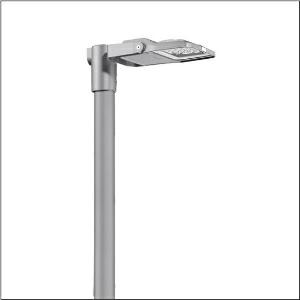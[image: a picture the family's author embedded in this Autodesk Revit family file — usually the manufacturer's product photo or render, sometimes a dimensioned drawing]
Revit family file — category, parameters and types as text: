
# Revit family: floodlight_fl_21_iq_micro___pl61_5xa7762a4c3a_196d
name_source: partatom
category: Lighting Fixtures
units: mm (PartAtom-declared; Revit-internal decimal feet)

## family parameters
Cut with Voids When Loaded = No
Host = Face
Light Source = No
Part Type = Normal
Room Calculation Point = No
Round Connector Dimension = Use Diameter
Shared = No

## types (1)
- --- (1 x LED, 3030 lm, 23.1 W, 4000K)
    Apparent Load = 23 VA
    CIE Flux Codes = 33 65 98 100 100
    Color Rendering = 70
    Color Temperature = 4000K
    Default Elevation = 1800 mm
    Description = Floodlight FL 21 iQ micro, floodlight, primary light control with lens, of PMMA, primary optical cover: protective disc, of toughened safety glass, transparent, light distribution: PL61, light emission: direct distribution, installation type: surface-mounted, lamps: LED, High Power LED, rated values: 3.030lm | 23,1W | 131,2lm/W (begin service life); end service life: 3.030lm | 23,8W; at 50% lumin. flux: 1.515lm | 11W | 137,7lm/W, colour temperature: 4000K, colour rendering: CRI > 70, light colour: 740, light setting 1 begin service life: 100% | 3.030lm | 23,1W | 131,2lm/W | 4.000K, light setting 1 end service life: 23,8W, further light settings possible, control: Auto-Match, Temp-Guard, Night-Set, Smart-Wire, Desk-Remote (wireless, voltage-free reading and setting of iQ features in the workshop via application-optimized NFC function/RFID function), optimised constant luminous flux control (CLO 2.0), Street-Remote, pre-setting: linear dimming characteristic, with terminal, 6-pole, mains connection: 220..240V, AC, 50/60Hz, luminaire housing, of diecast aluminium, powder-coated, SITECO metallic grey (DB 702S), corrosivity category C5 mid according to DIN EN ISO 12944suitable for swimming poolschlorine-resistant, sealing non-destructively replaceable, please order mast flange separately, mast bracket, of steel, galvanised, powder-coated, SITECO metallic grey (DB 702S), protection rating (complete): IP66, insulation class (complete): insulation class II (safety insulation), certification: CE, ENEC, VDE, protection symbol: D, impact resistance: IK07, permissible operating ambient temperature: -40..+40°C, permissible operating ambient temperature for outdoor applications: -40..+50°C, standard: DIN EN 12944, LABS conformity tested according to VDMA 24364:2018-05, packaging unit: 1 piece

Light Distribution: PL61
    Height = 65 mm
    Lamp = 1 x LED
    Lamp Light Flux = 3030 lm
    Lamp Power = 23.1 W
    Lamp count = 1
    Length = 312 mm
    Luminous efficacy = 131 lm/W
    Manufacturer = Siteco
    ModVariant = No
    Model = 5XA7762A4C3A
    Mounting Place = Pole
    Mounting Type = Pole annexe
    Number of Poles = 1
    OnlyDefault = Yes
    Power Factor = 1
    Product Name = Floodlight FL 21 iQ micro | PL61
    Product group = floodlight | pylon annexe
    ProductGroupID = 6201
    Protection Class = Protection class II
    Protection Degree = IP 66
    RLX_Detail_Level = 1
    RLX_Emergency_Light_Flux = 0 lm
    RLX_Emergency_Type = 0
    RLX_Emergency_Type_DB = No
    RlxData = <blob elided: 102161 chars, md5=10e7bd69>
    Socket = socket
    Standby Power = 0 W
    System Light Flux = 3030 lm
    System Power = 23 W
    Type Comments = factory setting: luminous flux: 100 % | dim-lin: 254 | 455 mA
    Type Image = l_1007121.jpg
    URL = http://relux.com
    VarID = @adj_193281
    Voltage = 0 V
    Weight = 0.00 kg
    Width = 230 mm

## geometry (parser evidence)
native form markers: Blend x4, Sweep x13
no freeform markers — native parametric forms only
